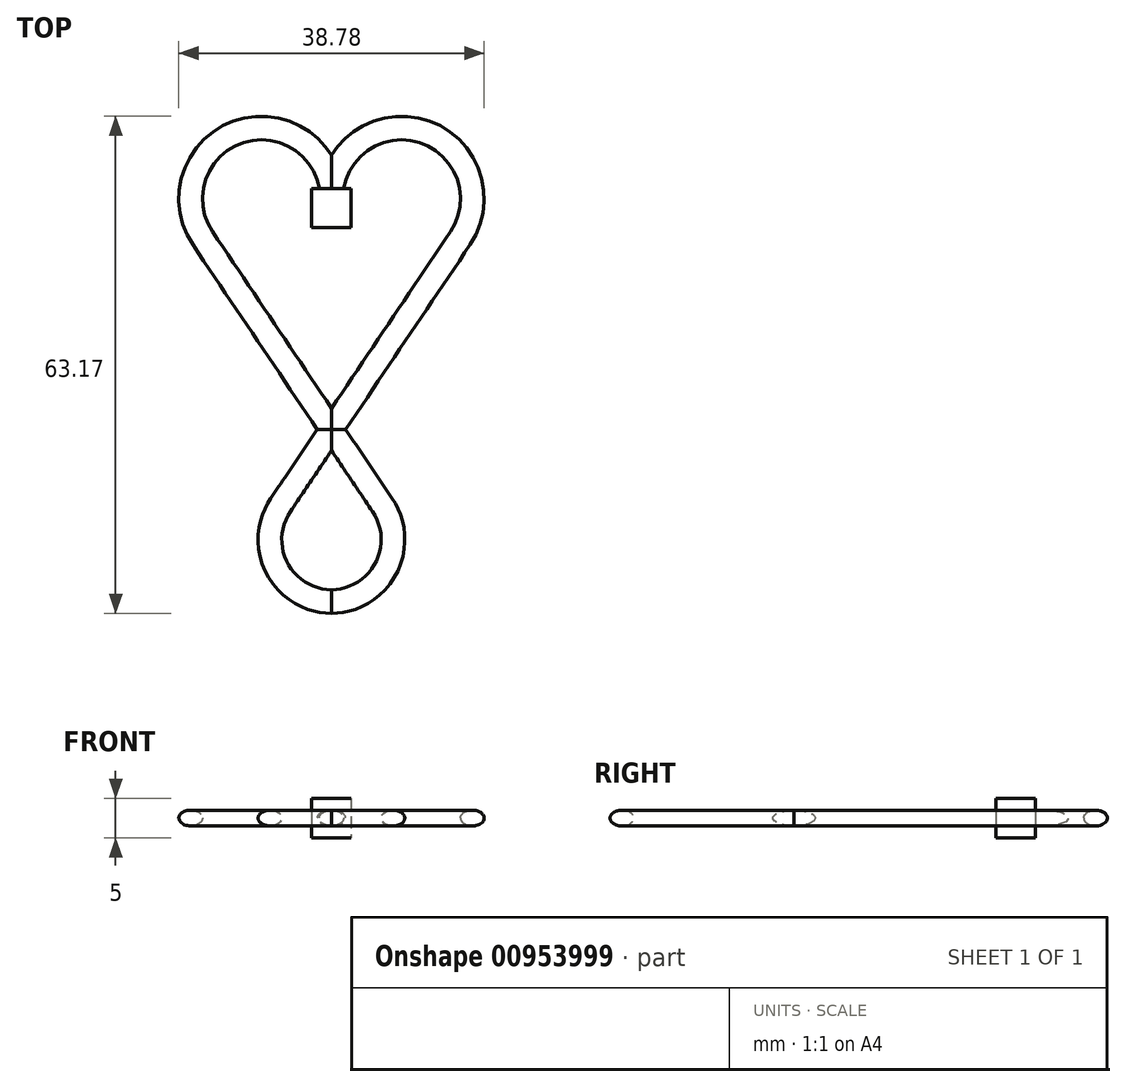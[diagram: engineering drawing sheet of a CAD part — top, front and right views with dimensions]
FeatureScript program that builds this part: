
annotation { "Feature Type Name" : "Feature", "Feature Type Description" : "" }
export const myFeature = defineFeature(function(context is Context, id is Id, definition is map)
    precondition{}
    {
        {
            var Q0;
            Q0=qCreatedBy(makeId("Top.planeOp"),FACE);
            var sketch = newSketch(context, id + "F0", { "sketchPlane" : qUnion([Q0])});
            skArc(sketch, "E0", {"start": v(16.36, 26.16) * mm, "mid": v(10.96, 39.93) * mm, "end": v(0, 30) * mm});
            skLineSegment(sketch, "E1", {"start": v(16.36, 26.16) * mm, "end": v(-6.47, -7.74) * mm});
            skArc(sketch, "E2", {"start": v(-6.47, -7.74) * mm, "mid": v(-6.9, -15.8) * mm, "end": v(0, -20) * mm});
            skLineSegment(sketch, "E3", {"start": v(16.36, 26.16) * mm, "end": v(16.36, 26.16) * mm});
            skSolve(sketch);
        }
        {
            var Q0;
            Q0=qCreatedBy(makeId("Right.planeOp"),FACE);
            var sketch = newSketch(context, id + "F1", { "sketchPlane" : qUnion([Q0])});
            skEllipse(sketch, "E4", {"center": v(-20, 0) * mm, "majorRadius": 1.5 * mm, "minorRadius": 1 * mm, "majorAxis": v(-1, 0)});
            skSolve(sketch);
        }
        {
            var Q0;
            Q0=makeQuery(id+"F1.imprint","IMPRINT",FACE,{"disambiguationData":[TD([[makeQuery(id+"F1.imprint","IMPRINT",EDGE,{"derivedFrom":sQuery(id+"F1.wireOp",EDGE,"E4")}),1.0]])]});
            var Q1;
            Q1=sQuery(id+"F0.wireOp",EDGE,"E2");
            var Q2;
            Q2=sQuery(id+"F0.wireOp",EDGE,"E1");
            var Q3;
            Q3=sQuery(id+"F0.wireOp",EDGE,"E0");
            sweep(context, id + "F2", {"profiles" : qUnion([Q0]), "path" : qUnion([Q1, Q2, Q3])});
        }
        {
            var Q0;
            Q0=makeQuery(id+"F2.opSweep","SWEPT_BODY",BODY,{"disambiguationData":[OSD([sQuery(id+"F0.wireOp",EDGE,"E0"),sQuery(id+"F1.wireOp",EDGE,"E4")])]});
            var Q1;
            Q1=qCreatedBy(makeId("Right.planeOp"),FACE);
            mirror(context, id + "F3", {"operationType" : NewBodyOperationType.ADD, "entities" : qUnion([Q0]), "mirrorPlane" : qUnion([Q1])});
        }
        {
            var Q0;
            Q0=qCreatedBy(makeId("Top.planeOp"),FACE);
            var sketch = newSketch(context, id + "F4", { "sketchPlane" : qUnion([Q0])});
            skLineSegment(sketch, "E5.bottom", {"start": v(-2.5, 27.5) * mm, "end": v(2.5, 27.5) * mm});
            skLineSegment(sketch, "E5.top", {"start": v(-2.5, 32.5) * mm, "end": v(2.5, 32.5) * mm});
            skLineSegment(sketch, "E5.left", {"start": v(-2.5, 27.5) * mm, "end": v(-2.5, 32.5) * mm});
            skLineSegment(sketch, "E5.right", {"start": v(2.5, 27.5) * mm, "end": v(2.5, 32.5) * mm});
            skPoint(sketch, "E5.middle", {"position": v(0, 30) * mm});
            skSolve(sketch);
        }
        {
            var Q0;
            Q0 = qSketchRegion(id + "F4", true);
            extrude(context, id + "F5", {"entities" : qUnion([Q0]), "operationType" : NewBodyOperationType.ADD, "endBound" : BoundingType.SYMMETRIC, "depth" : 5 * mm, "offsetDistance" : 25 * mm});
        }
    });
